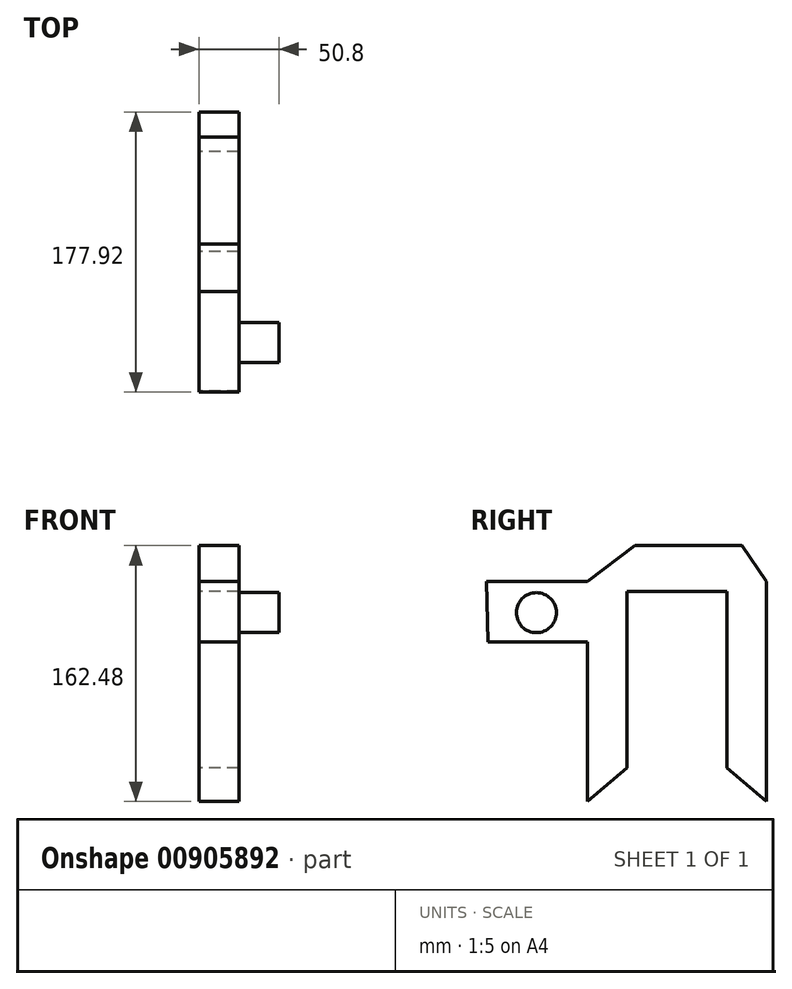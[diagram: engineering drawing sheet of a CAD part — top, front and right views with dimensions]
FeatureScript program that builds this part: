
annotation { "Feature Type Name" : "Feature", "Feature Type Description" : "" }
export const myFeature = defineFeature(function(context is Context, id is Id, definition is map)
    precondition{}
    {
        {
            var Q0;
            Q0=qCreatedBy(makeId("Right.planeOp"),FACE);
            var sketch = newSketch(context, id + "F0", { "sketchPlane" : qUnion([Q0])});
            skLineSegment(sketch, "E0", {"start": v(-89.2, 16.87) * mm, "end": v(-25.22, 16.87) * mm});
            skLineSegment(sketch, "E1", {"start": v(-25.22, 16.87) * mm, "end": v(4.95, 39.73) * mm});
            skLineSegment(sketch, "E2", {"start": v(4.95, 39.73) * mm, "end": v(72.95, 39.73) * mm});
            skLineSegment(sketch, "E3", {"start": v(72.95, 39.73) * mm, "end": v(88.72, 16.87) * mm});
            skLineSegment(sketch, "E4", {"start": v(88.72, 16.87) * mm, "end": v(88.72, -122.75) * mm});
            skLineSegment(sketch, "E5", {"start": v(88.72, -122.75) * mm, "end": v(63.5, -101.44) * mm});
            skLineSegment(sketch, "E6", {"start": v(63.5, -101.44) * mm, "end": v(63.5, 10.82) * mm});
            skLineSegment(sketch, "E7", {"start": v(63.5, 10.82) * mm, "end": v(0, 10.82) * mm});
            skLineSegment(sketch, "E8", {"start": v(0, 10.82) * mm, "end": v(0, -101.44) * mm});
            skLineSegment(sketch, "E9", {"start": v(0, -101.44) * mm, "end": v(-25.22, -122.75) * mm});
            skLineSegment(sketch, "E10", {"start": v(-25.22, -122.75) * mm, "end": v(-25.22, -21.36) * mm});
            skLineSegment(sketch, "E11", {"start": v(-25.22, -21.36) * mm, "end": v(-88.4, -21.36) * mm});
            skLineSegment(sketch, "E12", {"start": v(-88.4, -21.36) * mm, "end": v(-89.2, 16.87) * mm});
            skSolve(sketch);
        }
        {
            var Q0;
            Q0=makeQuery(id+"F0.imprint","IMPRINT",FACE,{"disambiguationData":[TD([[makeQuery(id+"F0.imprint","IMPRINT",EDGE,{"derivedFrom":sQuery(id+"F0.wireOp",EDGE,"E0")}),-1.0]])]});
            extrude(context, id + "F1", {"entities" : qUnion([Q0]), "depth" : 25.4 * mm, "offsetDistance" : 25.4 * mm});
        }
        {
            var Q0;
            Q0=makeQuery(id+"F1.opExtrude","CAP_FACE",FACE,{"disambiguationData":[OSD([sQuery(id+"F0.wireOp",EDGE,"E0"),sQuery(id+"F0.wireOp",EDGE,"E1"),sQuery(id+"F0.wireOp",EDGE,"E2"),sQuery(id+"F0.wireOp",EDGE,"E3"),sQuery(id+"F0.wireOp",EDGE,"E4"),sQuery(id+"F0.wireOp",EDGE,"E5"),sQuery(id+"F0.wireOp",EDGE,"E6"),sQuery(id+"F0.wireOp",EDGE,"E7"),sQuery(id+"F0.wireOp",EDGE,"E8"),sQuery(id+"F0.wireOp",EDGE,"E9"),sQuery(id+"F0.wireOp",EDGE,"E10"),sQuery(id+"F0.wireOp",EDGE,"E11"),sQuery(id+"F0.wireOp",EDGE,"E12")])],"isStart":false});
            var sketch = newSketch(context, id + "F2", { "sketchPlane" : qUnion([Q0])});
            skCircle(sketch, "E13", {"center": v(-57.53, -2.8) * mm, "radius": 12.7 * mm});
            skSolve(sketch);
        }
        {
            var Q0;
            Q0 = qSketchRegion(id + "F2", true);
            var Q1;
            Q1=sQuery(id+"F2.wireOp",EDGE,"E13");
            extrude(context, id + "F3", {"entities" : qUnion([Q0]), "operationType" : NewBodyOperationType.ADD, "surfaceEntities" : qUnion([Q1]), "depth" : 25.4 * mm, "offsetDistance" : 25.4 * mm});
        }
    });
